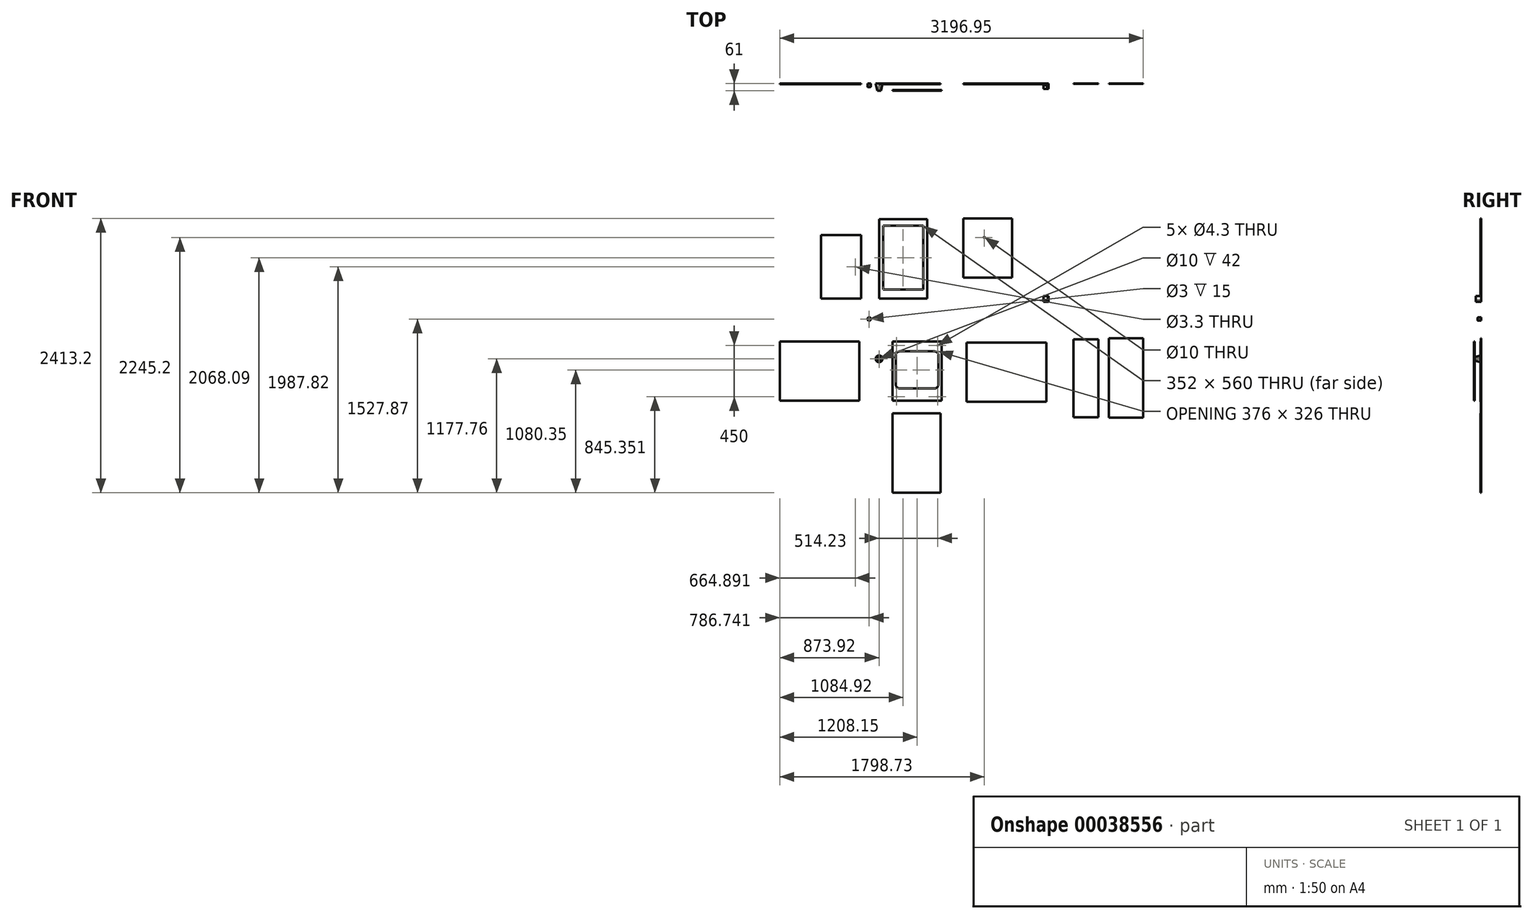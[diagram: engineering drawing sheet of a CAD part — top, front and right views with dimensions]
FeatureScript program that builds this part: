
annotation { "Feature Type Name" : "Feature", "Feature Type Description" : "" }
export const myFeature = defineFeature(function(context is Context, id is Id, definition is map)
    precondition{}
    {
        {
            assignVariable(context, id + "F0", {"name" : "tside", "anyValue" : 4});
        }
        {
            assignVariable(context, id + "F1", {"name" : "t_bottom", "anyValue" : 5});
        }
        {
            var Q0;
            Q0=qCreatedBy(makeId("Front.planeOp"),FACE);
            var sketch = newSketch(context, id + "F2", { "sketchPlane" : qUnion([Q0])});
            skCircle(sketch, "E0", {"center": v(0, 0) * mm, "radius": 30 * mm});
            skSolve(sketch);
        }
        {
            var Q0;
            Q0=makeQuery(id+"F2.imprint","IMPRINT",FACE,{"disambiguationData":[TD([[makeQuery(id+"F2.imprint","IMPRINT",EDGE,{"derivedFrom":sQuery(id+"F2.wireOp",EDGE,"E0")}),1.0]])]});
            cPlane(context, id + "F3", {"entities" : qUnion([Q0]), "cplaneType" : CPlaneType.OFFSET, "offset" : 61 * mm, "width" : 150 * mm, "height" : 150 * mm});
        }
        {
            var Q0;
            Q0=qCreatedBy(id+"F3.planeOp",FACE);
            var sketch = newSketch(context, id + "F4", { "sketchPlane" : qUnion([Q0])});
            skCircle(sketch, "E1", {"center": v(0, 0) * mm, "radius": 15 * mm});
            skSolve(sketch);
        }
        {
            var Q0;
            Q0=makeQuery(id+"F2.imprint","IMPRINT",FACE,{"disambiguationData":[TD([[makeQuery(id+"F2.imprint","IMPRINT",EDGE,{"derivedFrom":sQuery(id+"F2.wireOp",EDGE,"E0")}),1.0]])]});
            var Q1;
            Q1=makeQuery(id+"F4.imprint","IMPRINT",FACE,{"disambiguationData":[TD([[makeQuery(id+"F4.imprint","IMPRINT",EDGE,{"derivedFrom":sQuery(id+"F4.wireOp",EDGE,"E1")}),1.0]])]});
            loft(context, id + "F5", {"sheetProfilesArray" : [{ "sheetProfileEntities" : qUnion([Q0]) }, { "sheetProfileEntities" : qUnion([Q1]) }]});
        }
        {
            var Q0;
            Q0=makeQuery(id+"F5.opLoft","CAP_FACE",FACE,{"disambiguationData":[OSD([makeQuery(id+"F4.imprint","IMPRINT",FACE,{"disambiguationData":[TD([[makeQuery(id+"F4.imprint","IMPRINT",EDGE,{"derivedFrom":sQuery(id+"F4.wireOp",EDGE,"E1")}),1.0]])]})])],"isStart":true});
            var sketch = newSketch(context, id + "F6", { "sketchPlane" : qUnion([Q0])});
            skCircle(sketch, "E2", {"center": v(0, 0) * mm, "radius": 5 * mm});
            skSolve(sketch);
        }
        {
            var Q0;
            Q0=makeQuery(id+"F6.imprint","IMPRINT",FACE,{"disambiguationData":[TD([[makeQuery(id+"F6.imprint","IMPRINT",EDGE,{"derivedFrom":sQuery(id+"F6.wireOp",EDGE,"E2")}),1.0]])]});
            extrude(context, id + "F7", {"entities" : qUnion([Q0]), "operationType" : NewBodyOperationType.REMOVE, "oppositeDirection" : true, "depth" : 42 * mm});
        }
        {
            var Q0;
            Q0=makeQuery(id+"F7.boolean.opBoolean","COPY",FACE,{"derivedFrom":makeQuery(id+"F7.opExtrude","CAP_FACE",FACE,{"disambiguationData":[OSD([sQuery(id+"F6.wireOp",EDGE,"E2")])],"isStart":false})});
            var sketch = newSketch(context, id + "F8", { "sketchPlane" : qUnion([Q0])});
            skCircle(sketch, "E3", {"center": v(0, 0) * mm, "radius": 2.15 * mm});
            skSolve(sketch);
        }
        {
            var Q0;
            Q0=makeQuery(id+"F8.imprint","IMPRINT",FACE,{"disambiguationData":[TD([[makeQuery(id+"F8.imprint","IMPRINT",EDGE,{"derivedFrom":sQuery(id+"F8.wireOp",EDGE,"E3")}),1.0]])]});
            extrude(context, id + "F9", {"entities" : qUnion([Q0]), "operationType" : NewBodyOperationType.REMOVE, "endBound" : BoundingType.THROUGH_ALL, "oppositeDirection" : true, "depth" : 25 * mm});
        }
        {
            var Q0;
            Q0=qCreatedBy(id+"F3.planeOp",FACE);
            var sketch = newSketch(context, id + "F10", { "sketchPlane" : qUnion([Q0])});
            skLineSegment(sketch, "E4.bottom", {"start": v(119.23, 152.6) * mm, "end": v(549.23, 152.6) * mm});
            skLineSegment(sketch, "E4.top", {"start": v(119.23, -367.4) * mm, "end": v(549.23, -367.4) * mm});
            skLineSegment(sketch, "E4.left", {"start": v(119.23, 152.6) * mm, "end": v(119.23, -367.4) * mm});
            skLineSegment(sketch, "E4.right", {"start": v(549.23, 152.6) * mm, "end": v(549.23, -367.4) * mm});
            skCircle(sketch, "E5", {"center": v(154.23, 117.6) * mm, "radius": 30 * mm, "construction": true});
            skLineSegment(sketch, "E6", {"start": v(154.23, 152.6) * mm, "end": v(154.23, -367.4) * mm, "construction": true});
            skLineSegment(sketch, "E7", {"start": v(119.23, 117.6) * mm, "end": v(549.23, 117.6) * mm, "construction": true});
            skCircle(sketch, "E8", {"center": v(514.23, 117.6) * mm, "radius": 30 * mm, "construction": true});
            skCircle(sketch, "E9", {"center": v(514.23, -332.4) * mm, "radius": 30 * mm, "construction": true});
            skCircle(sketch, "E10", {"center": v(154.23, -332.4) * mm, "radius": 30 * mm, "construction": true});
            skLineSegment(sketch, "E11", {"start": v(119.23, -332.4) * mm, "end": v(549.23, -332.4) * mm, "construction": true});
            skLineSegment(sketch, "E12", {"start": v(514.23, 152.6) * mm, "end": v(514.23, -367.4) * mm, "construction": true});
            skCircle(sketch, "E13", {"center": v(154.23, 117.6) * mm, "radius": 2.15 * mm});
            skCircle(sketch, "E14", {"center": v(514.23, 117.6) * mm, "radius": 2.15 * mm});
            skCircle(sketch, "E15", {"center": v(514.23, -332.4) * mm, "radius": 2.15 * mm});
            skCircle(sketch, "E16", {"center": v(154.23, -332.4) * mm, "radius": 2.15 * mm});
            skSolve(sketch);
        }
        {
            var Q0;
            Q0=makeQuery(id+"F10.imprint","IMPRINT",FACE,{"disambiguationData":[TD([[makeQuery(id+"F10.imprint","IMPRINT",EDGE,{"derivedFrom":sQuery(id+"F10.wireOp",EDGE,"E4.bottom")}),-1.0]])]});
            extrude(context, id + "F11", {"entities" : qUnion([Q0]), "oppositeDirection" : true, "depth" : (getVariable(context, 't_bottom')) * mm});
        }
        {
            var Q0;
            Q0=makeQuery(id+"F11.opExtrude","CAP_FACE",FACE,{"disambiguationData":[OSD([sQuery(id+"F10.wireOp",EDGE,"E4.bottom"),sQuery(id+"F10.wireOp",EDGE,"E4.top"),sQuery(id+"F10.wireOp",EDGE,"E4.left"),sQuery(id+"F10.wireOp",EDGE,"E4.right")])],"isStart":true});
            var sketch = newSketch(context, id + "F12", { "sketchPlane" : qUnion([Q0])});
            skLineSegment(sketch, "E17.bottom", {"start": v(181.23, 65.6) * mm, "end": v(487.23, 65.6) * mm});
            skLineSegment(sketch, "E17.top", {"start": v(181.23, -260.4) * mm, "end": v(487.23, -260.4) * mm});
            skLineSegment(sketch, "E17.left", {"start": v(146.23, 30.6) * mm, "end": v(146.23, -225.4) * mm});
            skLineSegment(sketch, "E17.right", {"start": v(522.23, 30.6) * mm, "end": v(522.23, -225.4) * mm});
            skPoint(sketch, "E18.visualSharp", {"position": v(146.23, 65.6) * mm});
            skArc(sketch, "E18.filletArc", {"start": v(181.23, 65.6) * mm, "mid": v(156.48, 55.34) * mm, "end": v(146.23, 30.6) * mm});
            skPoint(sketch, "E19.visualSharp", {"position": v(522.23, 65.6) * mm});
            skArc(sketch, "E19.filletArc", {"start": v(522.23, 30.6) * mm, "mid": v(511.98, 55.34) * mm, "end": v(487.23, 65.6) * mm});
            skPoint(sketch, "E20.visualSharp", {"position": v(522.23, -260.4) * mm});
            skArc(sketch, "E20.filletArc", {"start": v(487.23, -260.4) * mm, "mid": v(511.98, -250.16) * mm, "end": v(522.23, -225.4) * mm});
            skPoint(sketch, "E21.visualSharp", {"position": v(146.23, -260.4) * mm});
            skArc(sketch, "E21.filletArc", {"start": v(146.23, -225.4) * mm, "mid": v(156.48, -250.16) * mm, "end": v(181.23, -260.4) * mm});
            skSolve(sketch);
        }
        {
            var Q0;
            Q0=makeQuery(id+"F12.imprint","IMPRINT",FACE,{"disambiguationData":[TD([[makeQuery(id+"F12.imprint","IMPRINT",EDGE,{"derivedFrom":sQuery(id+"F12.wireOp",EDGE,"E17.bottom")}),-1.0]])]});
            extrude(context, id + "F13", {"entities" : qUnion([Q0]), "operationType" : NewBodyOperationType.REMOVE, "endBound" : BoundingType.THROUGH_ALL, "oppositeDirection" : true, "depth" : 25 * mm});
        }
        {
            var Q0;
            Q0=qCreatedBy(makeId("Front.planeOp"),FACE);
            var sketch = newSketch(context, id + "F14", { "sketchPlane" : qUnion([Q0])});
            skLineSegment(sketch, "E22.bottom", {"start": v(-873.92, 152.6) * mm, "end": v(-173.92, 152.6) * mm});
            skLineSegment(sketch, "E22.top", {"start": v(-873.92, -367.4) * mm, "end": v(-173.92, -367.4) * mm});
            skLineSegment(sketch, "E22.left", {"start": v(-873.92, 152.6) * mm, "end": v(-873.92, -367.4) * mm});
            skLineSegment(sketch, "E22.right", {"start": v(-173.92, 152.6) * mm, "end": v(-173.92, -367.4) * mm});
            skLineSegment(sketch, "E23", {"start": v(119.23, -367.4) * mm, "end": v(-1076.8, -367.4) * mm, "construction": true});
            skSolve(sketch);
        }
        {
            var Q0;
            Q0=qCreatedBy(makeId("Front.planeOp"),FACE);
            var sketch = newSketch(context, id + "F15", { "sketchPlane" : qUnion([Q0])});
            skLineSegment(sketch, "E24.bottom", {"start": v(119.23, -477.76) * mm, "end": v(541.23, -477.76) * mm});
            skLineSegment(sketch, "E24.top", {"start": v(119.23, -1177.76) * mm, "end": v(541.23, -1177.76) * mm});
            skLineSegment(sketch, "E24.left", {"start": v(119.23, -477.76) * mm, "end": v(119.23, -1177.76) * mm});
            skLineSegment(sketch, "E24.right", {"start": v(541.23, -477.76) * mm, "end": v(541.23, -1177.76) * mm});
            skLineSegment(sketch, "E25", {"start": v(119.23, -367.4) * mm, "end": v(119.23, -1346.35) * mm, "construction": true});
            skSolve(sketch);
        }
        {
            var Q0;
            Q0=makeQuery(id+"F14.imprint","IMPRINT",FACE,{"disambiguationData":[TD([[makeQuery(id+"F14.imprint","IMPRINT",EDGE,{"derivedFrom":sQuery(id+"F14.wireOp",EDGE,"E22.bottom")}),-1.0]])]});
            extrude(context, id + "F16", {"entities" : qUnion([Q0]), "depth" : getVariable(context, 'tside') * mm});
        }
        {
            var Q0;
            Q0=makeQuery(id+"F15.imprint","IMPRINT",FACE,{"disambiguationData":[TD([[makeQuery(id+"F15.imprint","IMPRINT",EDGE,{"derivedFrom":sQuery(id+"F15.wireOp",EDGE,"E24.bottom")}),-1.0]])]});
            extrude(context, id + "F17", {"entities" : qUnion([Q0]), "depth" : (getVariable(context, 'tside')) * mm});
        }
        {
            var Q0;
            Q0=qCreatedBy(makeId("Front.planeOp"),FACE);
            var sketch = newSketch(context, id + "F18", { "sketchPlane" : qUnion([Q0])});
            skLineSegment(sketch, "E26.bottom", {"start": v(770.54, -376.42) * mm, "end": v(1470.54, -376.42) * mm});
            skLineSegment(sketch, "E26.top", {"start": v(770.54, 143.58) * mm, "end": v(1470.54, 143.58) * mm});
            skLineSegment(sketch, "E26.left", {"start": v(770.54, -376.42) * mm, "end": v(770.54, 143.58) * mm});
            skLineSegment(sketch, "E26.right", {"start": v(1470.54, -376.42) * mm, "end": v(1470.54, 143.58) * mm});
            skSolve(sketch);
        }
        {
            var Q0;
            Q0 = qSketchRegion(id + "F18", true);
            extrude(context, id + "F19", {"entities" : qUnion([Q0]), "depth" : (getVariable(context, 'tside')) * mm});
        }
        {
            var Q0;
            Q0=qCreatedBy(makeId("Front.planeOp"),FACE);
            var sketch = newSketch(context, id + "F20", { "sketchPlane" : qUnion([Q0])});
            skLineSegment(sketch, "E27.bottom", {"start": v(0, 1230.33) * mm, "end": v(422, 1230.33) * mm});
            skLineSegment(sketch, "E27.top", {"start": v(0, 530.33) * mm, "end": v(422, 530.33) * mm});
            skLineSegment(sketch, "E27.left", {"start": v(0, 1230.33) * mm, "end": v(0, 530.33) * mm});
            skLineSegment(sketch, "E27.right", {"start": v(422, 1230.33) * mm, "end": v(422, 530.33) * mm});
            skLineSegment(sketch, "E28.bottom", {"start": v(35, 610.33) * mm, "end": v(387, 610.33) * mm});
            skLineSegment(sketch, "E28.top", {"start": v(35, 1170.33) * mm, "end": v(387, 1170.33) * mm});
            skLineSegment(sketch, "E28.left", {"start": v(35, 610.33) * mm, "end": v(35, 1170.33) * mm});
            skLineSegment(sketch, "E28.right", {"start": v(387, 610.33) * mm, "end": v(387, 1170.33) * mm});
            skLineSegment(sketch, "E29", {"start": v(211, 530.33) * mm, "end": v(211, 1230.33) * mm, "construction": true});
            skSolve(sketch);
        }
        {
            var Q0;
            Q0=makeQuery(id+"F20.imprint","IMPRINT",FACE,{"disambiguationData":[TD([[makeQuery(id+"F20.imprint","IMPRINT",EDGE,{"derivedFrom":sQuery(id+"F20.wireOp",EDGE,"E27.bottom")}),-1.0]])]});
            extrude(context, id + "F21", {"entities" : qUnion([Q0]), "depth" : (getVariable(context, 'tside')) * mm});
        }
        {
            var Q0;
            Q0=qCreatedBy(makeId("Front.planeOp"),FACE);
            var sketch = newSketch(context, id + "F22", { "sketchPlane" : qUnion([Q0])});
            skLineSegment(sketch, "E30.bottom", {"start": v(739.81, 1235.44) * mm, "end": v(1169.81, 1235.44) * mm});
            skLineSegment(sketch, "E30.top", {"start": v(739.81, 715.44) * mm, "end": v(1169.81, 715.44) * mm});
            skLineSegment(sketch, "E30.left", {"start": v(739.81, 1235.44) * mm, "end": v(739.81, 715.44) * mm});
            skLineSegment(sketch, "E30.right", {"start": v(1169.81, 1235.44) * mm, "end": v(1169.81, 715.44) * mm});
            skLineSegment(sketch, "E31", {"start": v(954.81, 715.44) * mm, "end": v(954.81, 1235.44) * mm, "construction": true});
            skLineSegment(sketch, "E32", {"start": v(1169.81, 1067.44) * mm, "end": v(739.81, 1067.44) * mm, "construction": true});
            skCircle(sketch, "E33", {"center": v(924.81, 1067.44) * mm, "radius": 5 * mm});
            skLineSegment(sketch, "E34.bottom", {"start": v(899.81, 987.44) * mm, "end": v(1009.81, 987.44) * mm, "construction": true});
            skLineSegment(sketch, "E34.top", {"start": v(899.81, 857.44) * mm, "end": v(1009.81, 857.44) * mm, "construction": true});
            skLineSegment(sketch, "E34.left", {"start": v(899.81, 987.44) * mm, "end": v(899.81, 857.44) * mm, "construction": true});
            skLineSegment(sketch, "E34.right", {"start": v(1009.81, 987.44) * mm, "end": v(1009.81, 857.44) * mm, "construction": true});
            skSolve(sketch);
        }
        {
            var Q0;
            Q0=makeQuery(id+"F22.imprint","IMPRINT",FACE,{"disambiguationData":[TD([[makeQuery(id+"F22.imprint","IMPRINT",EDGE,{"derivedFrom":sQuery(id+"F22.wireOp",EDGE,"E30.bottom")}),-1.0]])]});
            extrude(context, id + "F23", {"entities" : qUnion([Q0]), "depth" : (getVariable(context, 't_bottom')) * mm});
        }
        {
            var Q0;
            Q0=qCreatedBy(makeId("Front.planeOp"),FACE);
            var sketch = newSketch(context, id + "F24", { "sketchPlane" : qUnion([Q0])});
            skLineSegment(sketch, "E35.bottom", {"start": v(-511.03, 1089.8) * mm, "end": v(-159.03, 1089.8) * mm});
            skLineSegment(sketch, "E35.top", {"start": v(-511.03, 530.3) * mm, "end": v(-159.03, 530.3) * mm});
            skLineSegment(sketch, "E35.left", {"start": v(-511.03, 1089.8) * mm, "end": v(-511.03, 530.3) * mm});
            skLineSegment(sketch, "E35.right", {"start": v(-159.03, 1089.8) * mm, "end": v(-159.03, 530.3) * mm});
            skCircle(sketch, "E36", {"center": v(-209.03, 810.06) * mm, "radius": 1.65 * mm});
            skLineSegment(sketch, "E37", {"start": v(-159.03, 810.06) * mm, "end": v(-511.03, 810.06) * mm, "construction": true});
            skSolve(sketch);
        }
        {
            var Q0;
            Q0=makeQuery(id+"F24.imprint","IMPRINT",FACE,{"disambiguationData":[TD([[makeQuery(id+"F24.imprint","IMPRINT",EDGE,{"derivedFrom":sQuery(id+"F24.wireOp",EDGE,"E35.bottom")}),-1.0]])]});
            extrude(context, id + "F25", {"entities" : qUnion([Q0]), "depth" : (getVariable(context, 'tside')) * mm});
        }
        {
            var Q0;
            Q0=qCreatedBy(makeId("Front.planeOp"),FACE);
            var sketch = newSketch(context, id + "F26", { "sketchPlane" : qUnion([Q0])});
            skCircle(sketch, "E38", {"center": v(-87.18, 350.1) * mm, "radius": 15 * mm});
            skSolve(sketch);
        }
        {
            var Q0;
            Q0=makeQuery(id+"F26.imprint","IMPRINT",FACE,{"disambiguationData":[TD([[makeQuery(id+"F26.imprint","IMPRINT",EDGE,{"derivedFrom":sQuery(id+"F26.wireOp",EDGE,"E38")}),1.0]])]});
            extrude(context, id + "F27", {"entities" : qUnion([Q0]), "depth" : 30 * mm});
        }
        {
            var Q0;
            Q0=makeQuery(id+"F27.opExtrude","CAP_EDGE",EDGE,{"disambiguationData":[OSD([sQuery(id+"F26.wireOp",EDGE,"E38")])],"isStart":false});
            fillet(context, id + "F28", {"entities" : qUnion([Q0]), "radius" : 5 * mm, "tangentPropagation" : true, "allowEdgeOverflow" : false});
        }
        {
            var Q0;
            Q0=makeQuery(id+"F27.opExtrude","CAP_FACE",FACE,{"disambiguationData":[OSD([sQuery(id+"F26.wireOp",EDGE,"E38")])],"isStart":true});
            var sketch = newSketch(context, id + "F29", { "sketchPlane" : qUnion([Q0])});
            skCircle(sketch, "E39", {"center": v(87.18, 350.1) * mm, "radius": 1.5 * mm});
            skSolve(sketch);
        }
        {
            var Q0;
            Q0=makeQuery(id+"F29.imprint","IMPRINT",FACE,{"disambiguationData":[TD([[makeQuery(id+"F29.imprint","IMPRINT",EDGE,{"derivedFrom":sQuery(id+"F29.wireOp",EDGE,"E39")}),1.0]])]});
            extrude(context, id + "F30", {"entities" : qUnion([Q0]), "operationType" : NewBodyOperationType.REMOVE, "oppositeDirection" : true, "depth" : 15 * mm});
        }
        {
            var Q0;
            Q0=qCreatedBy(makeId("Front.planeOp"),FACE);
            var sketch = newSketch(context, id + "F31", { "sketchPlane" : qUnion([Q0])});
            skLineSegment(sketch, "E40.bottom", {"start": v(1444.53, 551.42) * mm, "end": v(1484.53, 551.42) * mm});
            skLineSegment(sketch, "E40.top", {"start": v(1444.53, 511.42) * mm, "end": v(1484.53, 511.42) * mm});
            skLineSegment(sketch, "E40.left", {"start": v(1444.53, 551.42) * mm, "end": v(1444.53, 511.42) * mm});
            skLineSegment(sketch, "E40.right", {"start": v(1484.53, 551.42) * mm, "end": v(1484.53, 511.42) * mm});
            skSolve(sketch);
        }
        {
            var Q0;
            Q0=makeQuery(id+"F31.imprint","IMPRINT",FACE,{"disambiguationData":[TD([[makeQuery(id+"F31.imprint","IMPRINT",EDGE,{"derivedFrom":sQuery(id+"F31.wireOp",EDGE,"E40.bottom")}),-1.0]])]});
            extrude(context, id + "F32", {"entities" : qUnion([Q0]), "depth" : 5 * mm});
        }
        {
            var Q0;
            Q0=makeQuery(id+"F32.opExtrude","SWEPT_FACE",FACE,{"disambiguationData":[OSD([sQuery(id+"F31.wireOp",EDGE,"E40.right")])]});
            var sketch = newSketch(context, id + "F33", { "sketchPlane" : qUnion([Q0])});
            skLineSegment(sketch, "E41.bottom", {"start": v(0, 511.42) * mm, "end": v(-45, 511.42) * mm});
            skLineSegment(sketch, "E41.top", {"start": v(0, 551.42) * mm, "end": v(-45, 551.42) * mm});
            skLineSegment(sketch, "E41.left", {"start": v(0, 511.42) * mm, "end": v(0, 551.42) * mm});
            skLineSegment(sketch, "E41.right", {"start": v(-45, 511.42) * mm, "end": v(-45, 551.42) * mm});
            skSolve(sketch);
        }
        {
            var Q0;
            {var subQ1=sQuery(id+"F33.wireOp",EDGE,"E41.right");Q0=makeQuery(id+"F33.imprint","IMPRINT",FACE,{"disambiguationData":[TD([[makeQuery(id+"F33.imprint","IMPRINT",EDGE,{"derivedFrom":subQ1}),-1.0]])]});}
            var Q1;
            {var subQ1=sQuery(id+"F33.wireOp",EDGE,"E41.left");Q1=makeQuery(id+"F33.imprint","IMPRINT",FACE,{"disambiguationData":[TD([[makeQuery(id+"F33.imprint","IMPRINT",EDGE,{"derivedFrom":subQ1}),-1.0]])]});}
            extrude(context, id + "F34", {"entities" : qUnion([Q0, Q1]), "operationType" : NewBodyOperationType.ADD, "depth" : 5 * mm});
        }
        {
            var Q0;
            Q0=makeQuery(id+"F34.boolean.opBoolean","MERGE",FACE,{"derivedFrom":[makeQuery(id+"F32.opExtrude","SWEPT_FACE",FACE,{"disambiguationData":[OSD([sQuery(id+"F31.wireOp",EDGE,"E40.top")])]}),makeQuery(id+"F34.opExtrude","SWEPT_FACE",FACE,{"disambiguationData":[OSD([sQuery(id+"F33.wireOp",EDGE,"E41.bottom")])]})]});
            var sketch = newSketch(context, id + "F35", { "sketchPlane" : qUnion([Q0])});
            skPoint(sketch, "E42.oppositeSnap0", {"position": v(1444.53, 2.5) * mm});
            skLineSegment(sketch, "E42.bottom", {"start": v(1489.53, 0) * mm, "end": v(1444.53, 0) * mm});
            skLineSegment(sketch, "E42.top", {"start": v(1489.53, 45) * mm, "end": v(1444.53, 45) * mm});
            skLineSegment(sketch, "E42.left", {"start": v(1489.53, 0) * mm, "end": v(1489.53, 45) * mm});
            skLineSegment(sketch, "E42.right", {"start": v(1444.53, 0) * mm, "end": v(1444.53, 45) * mm});
            skSolve(sketch);
        }
        {
            var Q0;
            {var subQ2=sQuery(id+"F35.wireOp",EDGE,"E42.bottom");Q0=makeQuery(id+"F35.imprint","IMPRINT",FACE,{"disambiguationData":[TD([[makeQuery(id+"F35.imprint","IMPRINT",EDGE,{"derivedFrom":subQ2}),1.0]])]});}
            var Q1;
            {var subQ1=makeQuery(id+"F32.opExtrude","CAP_EDGE",EDGE,{"disambiguationData":[OSD([sQuery(id+"F31.wireOp",EDGE,"E40.top")])],"isStart":false});Q1=makeQuery(id+"F35.imprint","IMPRINT",FACE,{"disambiguationData":[TD([[makeQuery(id+"F35.imprint","IMPRINT",EDGE,{"derivedFrom":subQ1}),1.0]])]});}
            extrude(context, id + "F36", {"entities" : qUnion([Q0, Q1]), "operationType" : NewBodyOperationType.ADD, "depth" : 5 * mm});
        }
        {
            var Q0;
            Q0=makeQuery(id+"F36.opExtrude","CAP_FACE",FACE,{"disambiguationData":[OSD([sQuery(id+"F35.wireOp",EDGE,"E42.bottom"),sQuery(id+"F35.wireOp",EDGE,"E42.top"),sQuery(id+"F35.wireOp",EDGE,"E42.left"),sQuery(id+"F35.wireOp",EDGE,"E42.right")])],"isStart":false});
            var sketch = newSketch(context, id + "F37", { "sketchPlane" : qUnion([Q0])});
            skLineSegment(sketch, "E43", {"start": v(1489.53, 0) * mm, "end": v(1489.53, 45) * mm});
            skLineSegment(sketch, "E44", {"start": v(1489.53, 45) * mm, "end": v(1484.53, 45) * mm});
            skLineSegment(sketch, "E45", {"start": v(1484.53, 45) * mm, "end": v(1484.53, 5) * mm});
            skLineSegment(sketch, "E46", {"start": v(1484.53, 5) * mm, "end": v(1444.53, 5) * mm});
            skLineSegment(sketch, "E47", {"start": v(1444.53, 5) * mm, "end": v(1444.53, 0) * mm});
            skLineSegment(sketch, "E48", {"start": v(1444.53, 0) * mm, "end": v(1489.53, 0) * mm});
            skSolve(sketch);
        }
        {
            var Q0;
            Q0 = qSketchRegion(id + "F37", true);
            var Q1;
            Q1=makeQuery(id+"F36.opExtrude","CAP_FACE",FACE,{"disambiguationData":[OSD([sQuery(id+"F35.wireOp",EDGE,"E42.bottom"),sQuery(id+"F35.wireOp",EDGE,"E42.top"),sQuery(id+"F35.wireOp",EDGE,"E42.left"),sQuery(id+"F35.wireOp",EDGE,"E42.right")])],"isStart":true});
            extrude(context, id + "F38", {"entities" : qUnion([Q0, Q1]), "operationType" : NewBodyOperationType.ADD, "depth" : 5 * mm});
        }
        {
            var Q0;
            Q0=makeQuery(id+"F36.opExtrude","CAP_FACE",FACE,{"disambiguationData":[OSD([sQuery(id+"F35.wireOp",EDGE,"E42.bottom"),sQuery(id+"F35.wireOp",EDGE,"E42.top"),sQuery(id+"F35.wireOp",EDGE,"E42.left"),sQuery(id+"F35.wireOp",EDGE,"E42.right")])],"isStart":true});
            var sketch = newSketch(context, id + "F39", { "sketchPlane" : qUnion([Q0])});
            skLineSegment(sketch, "E49", {"start": v(1444.53, -8.5) * mm, "end": v(1481.03, -8.5) * mm});
            skLineSegment(sketch, "E50", {"start": v(1481.03, -8.5) * mm, "end": v(1481.03, -45) * mm});
            skLineSegment(sketch, "E51", {"start": v(1481.03, -45) * mm, "end": v(1476.03, -45) * mm});
            skLineSegment(sketch, "E52", {"start": v(1476.03, -45) * mm, "end": v(1476.03, -13.5) * mm});
            skLineSegment(sketch, "E53", {"start": v(1476.03, -13.5) * mm, "end": v(1444.53, -13.5) * mm});
            skLineSegment(sketch, "E54", {"start": v(1444.53, -13.5) * mm, "end": v(1444.53, -8.5) * mm});
            skSolve(sketch);
        }
        {
            var Q0;
            Q0=makeQuery(id+"F39.imprint","IMPRINT",FACE,{"disambiguationData":[TD([[makeQuery(id+"F39.imprint","IMPRINT",EDGE,{"derivedFrom":sQuery(id+"F39.wireOp",EDGE,"E49")}),-1.0]])]});
            extrude(context, id + "F40", {"entities" : qUnion([Q0]), "operationType" : NewBodyOperationType.ADD, "depth" : 5 * mm});
        }
        {
            var Q0;
            Q0=qCreatedBy(makeId("Front.planeOp"),FACE);
            var sketch = newSketch(context, id + "F41", { "sketchPlane" : qUnion([Q0])});
            skLineSegment(sketch, "E55.bottom", {"start": v(2021.03, 182.2) * mm, "end": v(2323.03, 182.2) * mm});
            skLineSegment(sketch, "E55.top", {"start": v(2021.03, -517.8) * mm, "end": v(2323.03, -517.8) * mm});
            skLineSegment(sketch, "E55.left", {"start": v(2021.03, 182.2) * mm, "end": v(2021.03, -517.8) * mm});
            skLineSegment(sketch, "E55.right", {"start": v(2323.03, 182.2) * mm, "end": v(2323.03, -517.8) * mm});
            skSolve(sketch);
        }
        {
            var Q0;
            Q0=makeQuery(id+"F41.imprint","IMPRINT",FACE,{"disambiguationData":[TD([[makeQuery(id+"F41.imprint","IMPRINT",EDGE,{"derivedFrom":sQuery(id+"F41.wireOp",EDGE,"E55.bottom")}),-1.0]])]});
            extrude(context, id + "F42", {"entities" : qUnion([Q0]), "depth" : 3 * mm});
        }
        {
            var Q0;
            Q0=qCreatedBy(makeId("Front.planeOp"),FACE);
            var sketch = newSketch(context, id + "F43", { "sketchPlane" : qUnion([Q0])});
            skLineSegment(sketch, "E56.bottom", {"start": v(1710.22, 170.97) * mm, "end": v(1928.22, 170.97) * mm});
            skLineSegment(sketch, "E56.top", {"start": v(1710.22, -514.03) * mm, "end": v(1928.22, -514.03) * mm});
            skLineSegment(sketch, "E56.left", {"start": v(1710.22, 170.97) * mm, "end": v(1710.22, -514.03) * mm});
            skLineSegment(sketch, "E56.right", {"start": v(1928.22, 170.97) * mm, "end": v(1928.22, -514.03) * mm});
            skSolve(sketch);
        }
        {
            var Q0;
            Q0=makeQuery(id+"F43.imprint","IMPRINT",FACE,{"disambiguationData":[TD([[makeQuery(id+"F43.imprint","IMPRINT",EDGE,{"derivedFrom":sQuery(id+"F43.wireOp",EDGE,"E56.bottom")}),-1.0]])]});
            extrude(context, id + "F44", {"entities" : qUnion([Q0]), "depth" : 3 * mm});
        }
    });
